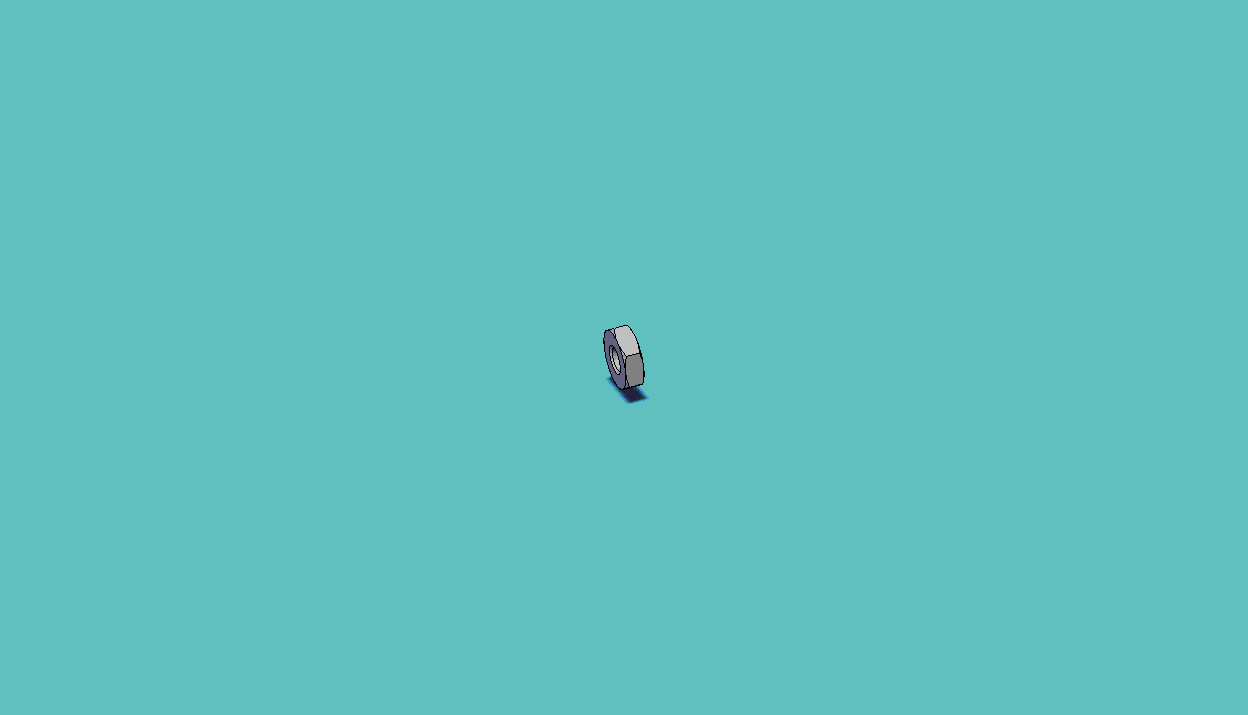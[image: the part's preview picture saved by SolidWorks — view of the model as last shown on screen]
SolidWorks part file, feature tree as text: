
SOLIDWORKS PART (.sldprt)
format: sldprt  version: not decoded by parser v0  size: 200,704 bytes
history: native  units: mm
features: sketch x4, plane x3, cut_revolve x3, material x1, extrude x1, thread x1, pattern_linear x1 + 2 further entries (+11 scaffold rows collapsed; 1 parser-record rows omitted)
feature tree (28):
  scaffold x11  (default folders/planes/origin — collapsed)
  material  "Material <not specified>"
  plane  "Plane1"
  plane  "Plane2"
  plane  "Plane3"
  parser-record x1  (decoder bookkeeping rows leaked as tree rows — omitted from the tree; the rows remain in map.json)
  cut_revolve  "EndChamfer"  [1 undecoded]
  sketch  "Sketch5"
  extrude  "BaseNut"  [1 undecoded]
  sketch  "BaseNutSke"  dims[c1.Tap_drill=2.05mm c1.D1=50.8mm c2.D1=30.0deg c2.D2=~24.797543mm c3.D2=60.0deg c3.D3=50.8mm c4.D3=30.0deg c4.D4=~24.797543mm c5.D4=60.0deg c6.D4=~24.797543mm c7.D4=60.0deg c8.D4=~24.797543mm c9.D4=60.0deg c9.Width_flats=5.0mm c9.D1=~21.475302mm c9.D2=~21.475302mm c10.D1=~21.475302mm c10.D2=2.5mm c10.D3=2.5mm c11.D1=~24.797543mm c12.D1=120.0deg c13.D1=~23.397294mm c14.D1=120.0deg c14.D4=2.5mm]
  thread  "ThreadCosmetic"  Diameter=2.5mm Thread_major=2.5mm Thickness=1.6mm  [1 undecoded]
  pattern_linear  "ThdSchPat"  [2 undecoded]
  cut_revolve  "ThreadSchematic"  [1 undecoded]
  sketch  "ThdSchSke"  dims[c1.D1=~4.490128mm c2.D1=90.0deg c3.D1=~4.490128mm c3.VeeAngle=70.0deg c4.D1=19.5834mm c4.SideAngle=55.0deg c5.D1=~4.490128mm c5.SideAngle=55.0deg c5.ThreadDepth=2.54mm c6.ThreadDepth=3.175mm c6.Thread_Major=6.35mm c6.D1=~9.573347mm c6.D2=~9.428305mm c6.OverCut=1.025mm c6.Tap_Drill=2.05mm c6.Advance=1.27mm c6.Thread_major=2.5mm c7.Advance=0.45mm c7.D1=6.35mm c7.D2=0.0254mm c8.D1=0.0254mm c9.D1=360.0deg c9.Num_threads=5.0 c9.Advance=0.3873mm c9.D2=1.0 c9.D4=50.0mm c10.D1=~8.980256mm c11.D1=315.0deg c12.D1=~8.980256mm c13.D1=45.0deg c13.D2=~8.94581mm c14.D2=~1.952549deg c14.D3=6.35mm c15.D2=25.7048mm c15.D1=~6.352235mm c16.D1=35.0deg c16.D2=12.7mm c16.D3=12.7mm c17.D2=22.5552mm c17.D3=25.4mm c17.D4=12.7mm c18.D3=12.7mm c18.D2=0.0508mm c18.Offset1=25.4254mm c18.ThreadMajor=12.7mm c18.ChamferDepth=0.2475mm c18.Offset2=1.6762mm c19.ThreadMajor=1.25mm c19.Offset1=1.6254mm c19.D1=360.0deg]
  sketch  "Sketch3"  dims[c1.D1=2.5mm c1.D2=2.4mm c1.D3=12.7mm c1.D4=10.0mm c1.D5=10.9093mm c1.D6=~10.998523mm c2.D6=~179.413404deg c3.D6=~2.539714mm c3.D3=10.0mm c3.D5=9.525mm c3.D2=~10.392305mm c4.D2=30.0deg]
  cut_revolve  "Double-Chamfer"  Angle=360deg
  "ConfigurationName"  CopiedFlag=1
  "ConfigurationName"  CopiedFlag=0
decode coverage: 5 of 10 modeling features carry decoded parameters; 2 rows unclassified (native names shown)
note: ~ marks probable driven/reference dimensions
note: 6 parameter values undecoded
summary: no parameter record found for 3 features
note: suppression state not decoded; provenance and decode notes live in map.json
